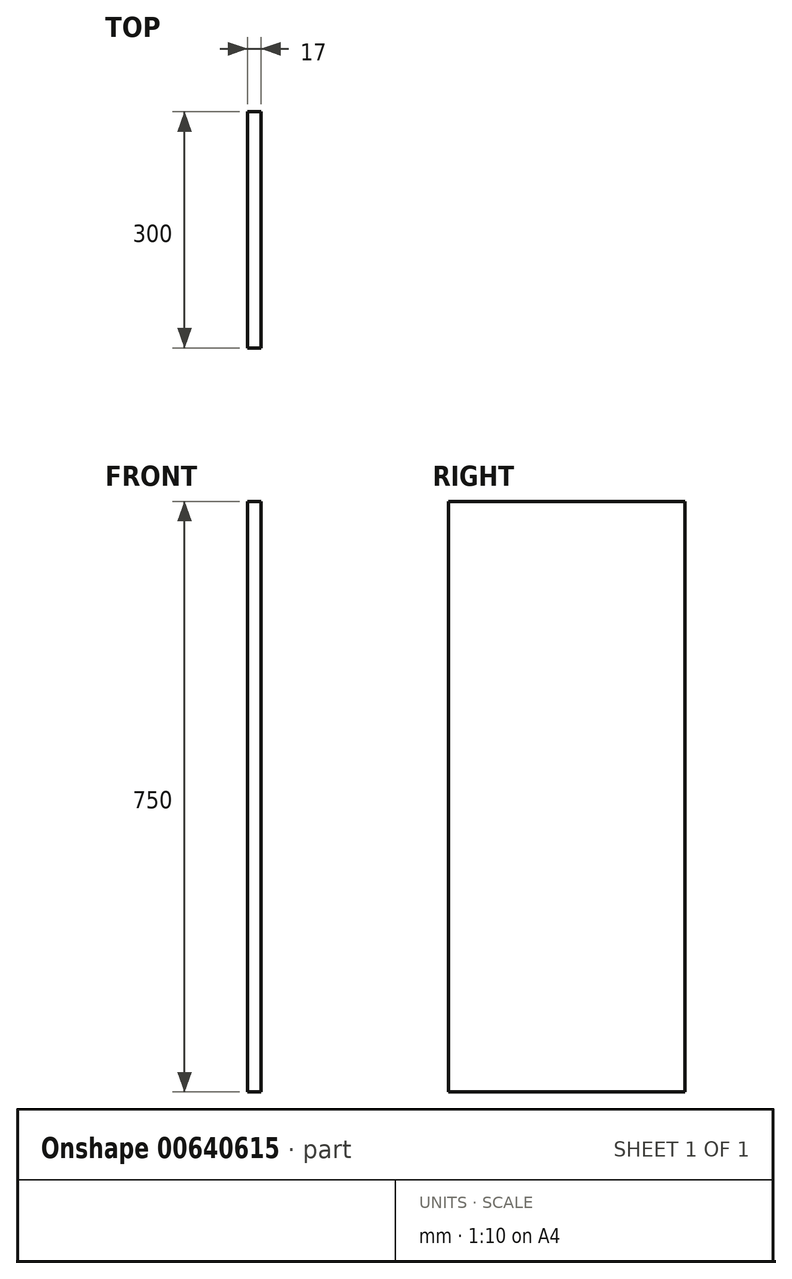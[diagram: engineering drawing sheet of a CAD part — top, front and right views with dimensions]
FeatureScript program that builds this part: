
annotation { "Feature Type Name" : "Feature", "Feature Type Description" : "" }
export const myFeature = defineFeature(function(context is Context, id is Id, definition is map)
    precondition{}
    {
        {
            var Q0;
            Q0=qCreatedBy(makeId("Right.planeOp"),FACE);
            var sketch = newSketch(context, id + "F0", { "sketchPlane" : qUnion([Q0])});
            skLineSegment(sketch, "E0.bottom", {"start": v(0, 0) * mm, "end": v(-300, 0) * mm});
            skLineSegment(sketch, "E0.top", {"start": v(0, 750) * mm, "end": v(-300, 750) * mm});
            skLineSegment(sketch, "E0.left", {"start": v(0, 0) * mm, "end": v(0, 750) * mm});
            skLineSegment(sketch, "E0.right", {"start": v(-300, 0) * mm, "end": v(-300, 750) * mm});
            skSolve(sketch);
        }
        {
            var Q0;
            Q0 = qSketchRegion(id + "F0", true);
            extrude(context, id + "F1", {"entities" : qUnion([Q0]), "oppositeDirection" : true, "depth" : 17 * mm, "offsetDistance" : 25 * mm});
        }
    });
